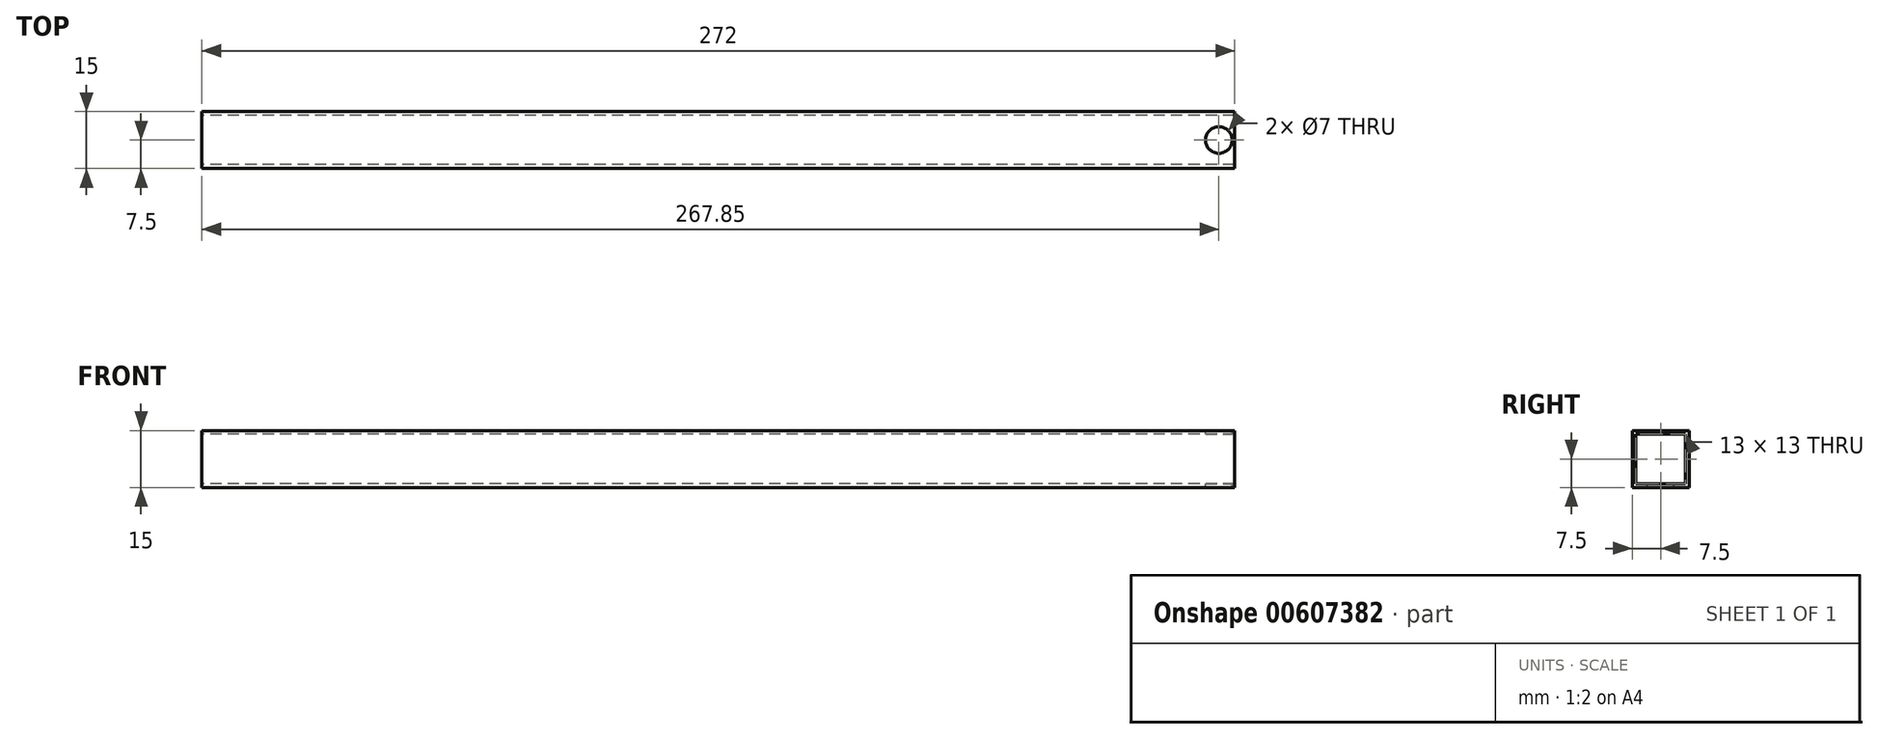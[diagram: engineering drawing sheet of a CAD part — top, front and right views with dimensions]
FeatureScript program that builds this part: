
annotation { "Feature Type Name" : "Feature", "Feature Type Description" : "" }
export const myFeature = defineFeature(function(context is Context, id is Id, definition is map)
    precondition{}
    {
        {
            var Q0;
            Q0=qCreatedBy(makeId("Right.planeOp"),FACE);
            var sketch = newSketch(context, id + "F0", { "sketchPlane" : qUnion([Q0])});
            skLineSegment(sketch, "E0.bottom", {"start": v(7.5, -7.5) * mm, "end": v(-7.5, -7.5) * mm});
            skLineSegment(sketch, "E0.top", {"start": v(7.5, 7.5) * mm, "end": v(-7.5, 7.5) * mm});
            skLineSegment(sketch, "E0.left", {"start": v(7.5, -7.5) * mm, "end": v(7.5, 7.5) * mm});
            skLineSegment(sketch, "E0.right", {"start": v(-7.5, -7.5) * mm, "end": v(-7.5, 7.5) * mm});
            skPoint(sketch, "E0.middle", {"position": v(0, 0) * mm});
            skLineSegment(sketch, "E1.bottom", {"start": v(6.5, -6.5) * mm, "end": v(-6.5, -6.5) * mm});
            skLineSegment(sketch, "E1.top", {"start": v(6.5, 6.5) * mm, "end": v(-6.5, 6.5) * mm});
            skLineSegment(sketch, "E1.left", {"start": v(6.5, -6.5) * mm, "end": v(6.5, 6.5) * mm});
            skLineSegment(sketch, "E1.right", {"start": v(-6.5, -6.5) * mm, "end": v(-6.5, 6.5) * mm});
            skSolve(sketch);
        }
        {
            var Q0;
            Q0 = qSketchRegion(id + "F0", true);
            extrude(context, id + "F1", {"entities" : qUnion([Q0]), "depth" : 136 * mm, "offsetDistance" : 25 * mm, "hasSecondDirection" : true, "secondDirectionOppositeDirection" : true, "secondDirectionDepth" : 136 * mm});
        }
        {
            var Q0;
            Q0=makeQuery(id+"F1.opExtrude","SWEPT_FACE",FACE,{"disambiguationData":[OSD([sQuery(id+"F0.wireOp",EDGE,"E0.top")])]});
            var sketch = newSketch(context, id + "F2", { "sketchPlane" : qUnion([Q0])});
            skCircle(sketch, "E2", {"center": v(131.85, 0) * mm, "radius": 3.5 * mm});
            skPoint(sketch, "E2.centerSnap0", {"position": v(136, 0) * mm});
            skSolve(sketch);
        }
        {
            var Q0;
            Q0=makeQuery(id+"F2.imprint","IMPRINT",FACE,{"disambiguationData":[TD([[makeQuery(id+"F2.imprint","IMPRINT",EDGE,{"derivedFrom":sQuery(id+"F2.wireOp",EDGE,"E2")}),1.0]])]});
            extrude(context, id + "F3", {"entities" : qUnion([Q0]), "operationType" : NewBodyOperationType.REMOVE, "oppositeDirection" : true, "depth" : 25 * mm, "offsetDistance" : 25 * mm});
        }
    });
